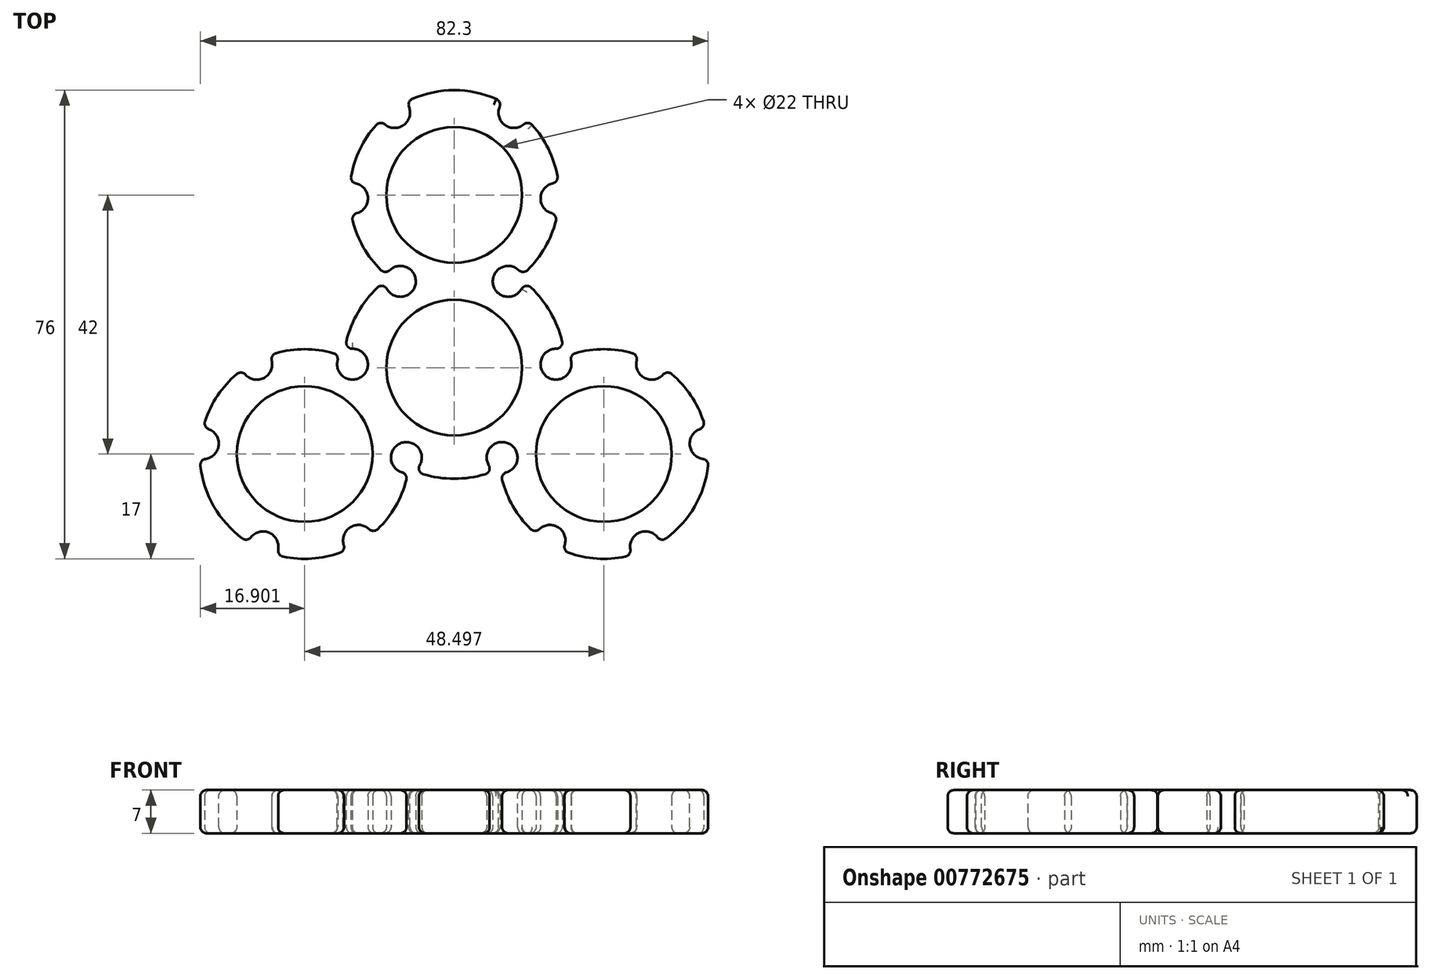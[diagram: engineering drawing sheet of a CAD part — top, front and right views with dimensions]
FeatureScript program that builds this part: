
annotation { "Feature Type Name" : "Feature", "Feature Type Description" : "" }
export const myFeature = defineFeature(function(context is Context, id is Id, definition is map)
    precondition{}
    {
        {
            var Q0;
            Q0=qCreatedBy(makeId("Top.planeOp"),FACE);
            var sketch = newSketch(context, id + "F0", { "sketchPlane" : qUnion([Q0])});
            skCircle(sketch, "E0", {"center": v(0, 0) * mm, "radius": 11 * mm});
            skCircle(sketch, "E1", {"center": v(0, 28) * mm, "radius": 11 * mm});
            skCircle(sketch, "E2", {"center": v(24.25, -14) * mm, "radius": 11 * mm});
            skCircle(sketch, "E3", {"center": v(-24.25, -14) * mm, "radius": 11 * mm});
            skLineSegment(sketch, "E4", {"start": v(0, 0) * mm, "end": v(0, 77.87) * mm, "construction": true});
            skLineSegment(sketch, "E5", {"start": v(0, 0) * mm, "end": v(69.01, -39.84) * mm, "construction": true});
            skLineSegment(sketch, "E6", {"start": v(0, 0) * mm, "end": v(-61.15, -35.3) * mm, "construction": true});
            skCircle(sketch, "E7", {"center": v(0, 0) * mm, "radius": 14 * mm});
            skCircle(sketch, "E8", {"center": v(0, 28) * mm, "radius": 14 * mm});
            skCircle(sketch, "E9", {"center": v(24.25, -14) * mm, "radius": 14 * mm});
            skCircle(sketch, "E10", {"center": v(-24.25, -14) * mm, "radius": 14 * mm});
            skArc(sketch, "E11", {"start": v(7.4, 16.12) * mm, "mid": v(6.23, 14) * mm, "end": v(7.4, 11.88) * mm});
            skArc(sketch, "E12", {"start": v(-7.4, 11.88) * mm, "mid": v(-6.23, 14) * mm, "end": v(-7.4, 16.12) * mm});
            skArc(sketch, "E13.1.0", {"start": v(-6.58, -12.36) * mm, "mid": v(-9, -12.4) * mm, "end": v(-10.26, -14.48) * mm});
            skArc(sketch, "E13.1.1", {"start": v(-17.67, -1.64) * mm, "mid": v(-15.24, -1.6) * mm, "end": v(-14, 0.48) * mm});
            skArc(sketch, "E13.2.0", {"start": v(14, 0.48) * mm, "mid": v(15.24, -1.6) * mm, "end": v(17.67, -1.64) * mm});
            skArc(sketch, "E13.2.1", {"start": v(10.26, -14.48) * mm, "mid": v(9, -12.4) * mm, "end": v(6.58, -12.36) * mm});
            skSolve(sketch);
        }
        {
            var Q0;
            Q0 = qSketchRegion(id + "F0", true);
            extrude(context, id + "F1", {"entities" : qUnion([Q0]), "depth" : 7 * mm, "offsetDistance" : 25 * mm});
        }
        {
            var Q0;
            Q0=makeQuery(id+"F1.opExtrude","CAP_FACE",FACE,{"disambiguationData":[OSD([sQuery(id+"F0.wireOp",EDGE,"E0"),sQuery(id+"F0.wireOp",EDGE,"E1"),sQuery(id+"F0.wireOp",EDGE,"E2"),sQuery(id+"F0.wireOp",EDGE,"E3"),sQuery(id+"F0.wireOp",EDGE,"E7"),sQuery(id+"F0.wireOp",EDGE,"E8"),sQuery(id+"F0.wireOp",EDGE,"E9"),sQuery(id+"F0.wireOp",EDGE,"E10"),sQuery(id+"F0.wireOp",EDGE,"E11"),sQuery(id+"F0.wireOp",EDGE,"E12"),sQuery(id+"F0.wireOp",EDGE,"E13.1.0"),sQuery(id+"F0.wireOp",EDGE,"E13.1.1"),sQuery(id+"F0.wireOp",EDGE,"E13.2.0"),sQuery(id+"F0.wireOp",EDGE,"E13.2.1")])],"isStart":false});
            var sketch = newSketch(context, id + "F2", { "sketchPlane" : qUnion([Q0])});
            skArc(sketch, "E14", {"start": v(7.4, 11.88) * mm, "mid": v(9.97, 11.83) * mm, "end": v(11.23, 14.07) * mm});
            skArc(sketch, "E15", {"start": v(17.8, 2.7) * mm, "mid": v(15.23, 2.72) * mm, "end": v(14, 0.48) * mm});
            skArc(sketch, "E16", {"start": v(17.8, 2.7) * mm, "mid": v(15.59, 9) * mm, "end": v(11.23, 14.07) * mm});
            skArc(sketch, "E17.1.0", {"start": v(-14, 0.48) * mm, "mid": v(-15.23, 2.72) * mm, "end": v(-17.8, 2.7) * mm});
            skArc(sketch, "E17.1.1", {"start": v(-11.23, 14.07) * mm, "mid": v(-15.59, 9) * mm, "end": v(-17.8, 2.7) * mm});
            skArc(sketch, "E17.1.2", {"start": v(-11.23, 14.07) * mm, "mid": v(-9.97, 11.83) * mm, "end": v(-7.4, 11.88) * mm});
            skArc(sketch, "E17.2.0", {"start": v(6.58, -12.36) * mm, "mid": v(5.26, -14.55) * mm, "end": v(6.57, -16.76) * mm});
            skArc(sketch, "E17.2.1", {"start": v(-6.57, -16.76) * mm, "mid": v(0, -18) * mm, "end": v(6.57, -16.76) * mm});
            skArc(sketch, "E17.2.2", {"start": v(-6.57, -16.76) * mm, "mid": v(-5.26, -14.55) * mm, "end": v(-6.58, -12.36) * mm});
            skCircle(sketch, "E18", {"center": v(0, 0) * mm, "radius": 14 * mm});
            skCircle(sketch, "E19", {"center": v(0, 0) * mm, "radius": 11.43 * mm});
            skSolve(sketch);
        }
        {
            var Q0;
            Q0 = qSketchRegion(id + "F2", true);
            extrude(context, id + "F3", {"entities" : qUnion([Q0]), "operationType" : NewBodyOperationType.ADD, "oppositeDirection" : true, "depth" : 7 * mm, "offsetDistance" : 25 * mm});
        }
        {
            var Q0;
            Q0=makeQuery(id+"F3.opExtrude","SWEPT_EDGE",EDGE,{"disambiguationData":[OSD([sQuery(id+"F2.wireOp",EDGE,"E17.1.1"),sQuery(id+"F2.wireOp",EDGE,"E17.1.2")])]});
            var Q1;
            Q1=makeQuery(id+"F3.opExtrude","SWEPT_EDGE",EDGE,{"disambiguationData":[OSD([sQuery(id+"F2.wireOp",EDGE,"E17.1.0"),sQuery(id+"F2.wireOp",EDGE,"E17.1.1")])]});
            var Q2;
            Q2=makeQuery(id+"F3.opExtrude","SWEPT_EDGE",EDGE,{"disambiguationData":[OSD([sQuery(id+"F2.wireOp",EDGE,"E17.2.1"),sQuery(id+"F2.wireOp",EDGE,"E17.2.2")])]});
            var Q3;
            Q3=makeQuery(id+"F3.opExtrude","SWEPT_EDGE",EDGE,{"disambiguationData":[OSD([sQuery(id+"F2.wireOp",EDGE,"E17.2.0"),sQuery(id+"F2.wireOp",EDGE,"E17.2.1")])]});
            var Q4;
            Q4=makeQuery(id+"F3.opExtrude","SWEPT_EDGE",EDGE,{"disambiguationData":[OSD([sQuery(id+"F2.wireOp",EDGE,"E15"),sQuery(id+"F2.wireOp",EDGE,"E16")])]});
            var Q5;
            Q5=makeQuery(id+"F3.opExtrude","SWEPT_EDGE",EDGE,{"disambiguationData":[OSD([sQuery(id+"F2.wireOp",EDGE,"E14"),sQuery(id+"F2.wireOp",EDGE,"E16")])]});
            fillet(context, id + "F4", {"entities" : qUnion([Q0, Q1, Q2, Q3, Q4, Q5]), "radius" : 1 * mm, "tangentPropagation" : true, "allowEdgeOverflow" : false});
        }
        {
            var Q0;
            Q0=makeQuery(id+"F3.boolean.opBoolean","MERGE",FACE,{"derivedFrom":[makeQuery(id+"F1.opExtrude","CAP_FACE",FACE,{"disambiguationData":[OSD([sQuery(id+"F0.wireOp",EDGE,"E0"),sQuery(id+"F0.wireOp",EDGE,"E1"),sQuery(id+"F0.wireOp",EDGE,"E2"),sQuery(id+"F0.wireOp",EDGE,"E3"),sQuery(id+"F0.wireOp",EDGE,"E7"),sQuery(id+"F0.wireOp",EDGE,"E8"),sQuery(id+"F0.wireOp",EDGE,"E9"),sQuery(id+"F0.wireOp",EDGE,"E10"),sQuery(id+"F0.wireOp",EDGE,"E11"),sQuery(id+"F0.wireOp",EDGE,"E12"),sQuery(id+"F0.wireOp",EDGE,"E13.1.0"),sQuery(id+"F0.wireOp",EDGE,"E13.1.1"),sQuery(id+"F0.wireOp",EDGE,"E13.2.0"),sQuery(id+"F0.wireOp",EDGE,"E13.2.1")])],"isStart":false}),makeQuery(id+"F3.opExtrude","CAP_FACE",FACE,{"disambiguationData":[OSD([sQuery(id+"F2.wireOp",EDGE,"E14"),sQuery(id+"F2.wireOp",EDGE,"E15"),sQuery(id+"F2.wireOp",EDGE,"E16"),sQuery(id+"F2.wireOp",EDGE,"E17.1.0"),sQuery(id+"F2.wireOp",EDGE,"E17.1.1"),sQuery(id+"F2.wireOp",EDGE,"E17.1.2"),sQuery(id+"F2.wireOp",EDGE,"E17.2.0"),sQuery(id+"F2.wireOp",EDGE,"E17.2.1"),sQuery(id+"F2.wireOp",EDGE,"E17.2.2"),sQuery(id+"F2.wireOp",EDGE,"E18"),sQuery(id+"F2.wireOp",EDGE,"E19")])],"isStart":true})]});
            var sketch = newSketch(context, id + "F5", { "sketchPlane" : qUnion([Q0])});
            skArc(sketch, "E20", {"start": v(-7.4, 16.12) * mm, "mid": v(-9.45, 16.4) * mm, "end": v(-11, 15.04) * mm});
            skArc(sketch, "E21", {"start": v(-16.72, 24.95) * mm, "mid": v(-14.78, 25.62) * mm, "end": v(-14, 27.52) * mm});
            skArc(sketch, "E22", {"start": v(-16.72, 24.95) * mm, "mid": v(-14.72, 19.5) * mm, "end": v(-11, 15.04) * mm});
            skArc(sketch, "E23.2.0", {"start": v(14, 27.52) * mm, "mid": v(14.78, 25.62) * mm, "end": v(16.72, 24.95) * mm});
            skArc(sketch, "E23.2.1", {"start": v(11, 15.04) * mm, "mid": v(14.72, 19.5) * mm, "end": v(16.72, 24.95) * mm});
            skArc(sketch, "E23.2.2", {"start": v(11, 15.04) * mm, "mid": v(9.45, 16.4) * mm, "end": v(7.4, 16.12) * mm});
            skArc(sketch, "E24", {"start": v(-7.4, 16.12) * mm, "mid": v(0, 14) * mm, "end": v(7.4, 16.12) * mm});
            skCircle(sketch, "E25", {"center": v(0, 28) * mm, "radius": 11.73 * mm});
            skArc(sketch, "E26", {"start": v(-14, 27.52) * mm, "mid": v(-14.9, 29.37) * mm, "end": v(-16.9, 29.9) * mm});
            skArc(sketch, "E27", {"start": v(16.9, 29.9) * mm, "mid": v(14.9, 29.37) * mm, "end": v(14, 27.52) * mm});
            skArc(sketch, "E28", {"start": v(-11.86, 40.18) * mm, "mid": v(-10.22, 38.94) * mm, "end": v(-8.2, 39.35) * mm});
            skArc(sketch, "E29", {"start": v(8.2, 39.35) * mm, "mid": v(10.22, 38.94) * mm, "end": v(11.86, 40.18) * mm});
            skArc(sketch, "E30", {"start": v(-11.86, 40.18) * mm, "mid": v(-15.27, 35.48) * mm, "end": v(-16.9, 29.9) * mm});
            skArc(sketch, "E31", {"start": v(16.9, 29.9) * mm, "mid": v(15.27, 35.48) * mm, "end": v(11.86, 40.18) * mm});
            skArc(sketch, "E32", {"start": v(7.84, 43.08) * mm, "mid": v(7.18, 41.13) * mm, "end": v(8.2, 39.35) * mm});
            skArc(sketch, "E33", {"start": v(-8.2, 39.35) * mm, "mid": v(-7.18, 41.13) * mm, "end": v(-7.84, 43.08) * mm});
            skArc(sketch, "E34", {"start": v(7.84, 43.08) * mm, "mid": v(0, 45) * mm, "end": v(-7.84, 43.08) * mm});
            skArc(sketch, "E35.1.0", {"start": v(-28.87, -30.36) * mm, "mid": v(-23.1, -30.96) * mm, "end": v(-17.45, -29.58) * mm});
            skCircle(sketch, "E35.1.1", {"center": v(-24.25, -14) * mm, "radius": 11.73 * mm});
            skArc(sketch, "E35.1.2", {"start": v(-28.87, -30.36) * mm, "mid": v(-28.6, -28.32) * mm, "end": v(-29.98, -26.78) * mm});
            skArc(sketch, "E35.1.3", {"start": v(-29.98, -26.78) * mm, "mid": v(-32.04, -26.78) * mm, "end": v(-33.4, -28.33) * mm});
            skArc(sketch, "E35.1.4", {"start": v(-41.23, -14.75) * mm, "mid": v(-38.97, -22.5) * mm, "end": v(-33.4, -28.33) * mm});
            skArc(sketch, "E35.1.5", {"start": v(-41.23, -14.75) * mm, "mid": v(-39.21, -14.35) * mm, "end": v(-38.18, -12.57) * mm});
            skArc(sketch, "E35.1.6", {"start": v(-38.18, -12.57) * mm, "mid": v(-38.83, -10.62) * mm, "end": v(-40.73, -9.82) * mm});
            skArc(sketch, "E35.1.7", {"start": v(-34.35, -0.32) * mm, "mid": v(-38.36, -4.52) * mm, "end": v(-40.73, -9.82) * mm});
            skArc(sketch, "E35.1.8", {"start": v(-34.35, -0.32) * mm, "mid": v(-32.89, -1.78) * mm, "end": v(-30.83, -1.64) * mm});
            skArc(sketch, "E35.1.9", {"start": v(-30.83, -1.64) * mm, "mid": v(-29.57, -0.01) * mm, "end": v(-29.97, 2) * mm});
            skArc(sketch, "E35.1.10", {"start": v(-18.53, 2) * mm, "mid": v(-24.25, 3) * mm, "end": v(-29.97, 2) * mm});
            skArc(sketch, "E35.1.11", {"start": v(-18.53, 2) * mm, "mid": v(-18.92, -0.01) * mm, "end": v(-17.67, -1.64) * mm});
            skArc(sketch, "E35.1.12", {"start": v(-10.26, -14.48) * mm, "mid": v(-12.12, -7) * mm, "end": v(-17.67, -1.64) * mm});
            skArc(sketch, "E35.1.13", {"start": v(-10.26, -14.48) * mm, "mid": v(-9.47, -16.38) * mm, "end": v(-7.52, -17.05) * mm});
            skArc(sketch, "E35.1.14", {"start": v(-13.24, -26.96) * mm, "mid": v(-9.53, -22.5) * mm, "end": v(-7.52, -17.05) * mm});
            skArc(sketch, "E35.1.15", {"start": v(-13.24, -26.96) * mm, "mid": v(-14.8, -25.6) * mm, "end": v(-16.84, -25.88) * mm});
            skArc(sketch, "E35.1.16", {"start": v(-16.84, -25.88) * mm, "mid": v(-17.98, -27.6) * mm, "end": v(-17.45, -29.58) * mm});
            skArc(sketch, "E35.2.0", {"start": v(40.73, -9.82) * mm, "mid": v(38.36, -4.52) * mm, "end": v(34.35, -0.32) * mm});
            skCircle(sketch, "E35.2.1", {"center": v(24.25, -14) * mm, "radius": 11.73 * mm});
            skArc(sketch, "E35.2.2", {"start": v(40.73, -9.82) * mm, "mid": v(38.83, -10.62) * mm, "end": v(38.18, -12.57) * mm});
            skArc(sketch, "E35.2.3", {"start": v(38.18, -12.57) * mm, "mid": v(39.21, -14.35) * mm, "end": v(41.23, -14.75) * mm});
            skArc(sketch, "E35.2.4", {"start": v(33.4, -28.33) * mm, "mid": v(38.97, -22.5) * mm, "end": v(41.23, -14.75) * mm});
            skArc(sketch, "E35.2.5", {"start": v(33.4, -28.33) * mm, "mid": v(32.03, -26.78) * mm, "end": v(29.98, -26.78) * mm});
            skArc(sketch, "E35.2.6", {"start": v(29.98, -26.78) * mm, "mid": v(28.6, -28.32) * mm, "end": v(28.86, -30.36) * mm});
            skArc(sketch, "E35.2.7", {"start": v(17.45, -29.58) * mm, "mid": v(23.1, -30.96) * mm, "end": v(28.86, -30.36) * mm});
            skArc(sketch, "E35.2.8", {"start": v(17.45, -29.58) * mm, "mid": v(17.98, -27.6) * mm, "end": v(16.84, -25.88) * mm});
            skArc(sketch, "E35.2.9", {"start": v(16.84, -25.88) * mm, "mid": v(14.8, -25.6) * mm, "end": v(13.24, -26.96) * mm});
            skArc(sketch, "E35.2.10", {"start": v(7.52, -17.05) * mm, "mid": v(9.53, -22.5) * mm, "end": v(13.24, -26.96) * mm});
            skArc(sketch, "E35.2.11", {"start": v(7.52, -17.05) * mm, "mid": v(9.47, -16.38) * mm, "end": v(10.26, -14.48) * mm});
            skArc(sketch, "E35.2.12", {"start": v(17.67, -1.64) * mm, "mid": v(12.12, -7) * mm, "end": v(10.26, -14.48) * mm});
            skArc(sketch, "E35.2.13", {"start": v(17.67, -1.64) * mm, "mid": v(18.92, -0.01) * mm, "end": v(18.53, 2) * mm});
            skArc(sketch, "E35.2.14", {"start": v(29.97, 2) * mm, "mid": v(24.25, 3) * mm, "end": v(18.53, 2) * mm});
            skArc(sketch, "E35.2.15", {"start": v(29.97, 2) * mm, "mid": v(29.57, -0.01) * mm, "end": v(30.83, -1.64) * mm});
            skArc(sketch, "E35.2.16", {"start": v(30.83, -1.64) * mm, "mid": v(32.89, -1.78) * mm, "end": v(34.35, -0.32) * mm});
            skPoint(sketch, "E35.center", {"position": v(0, 0) * mm});
            skSolve(sketch);
        }
        {
            var Q0;
            Q0 = qSketchRegion(id + "F5", true);
            extrude(context, id + "F6", {"entities" : qUnion([Q0]), "operationType" : NewBodyOperationType.ADD, "oppositeDirection" : true, "depth" : 7 * mm, "offsetDistance" : 25 * mm});
        }
        {
            var Q0;
            Q0=makeQuery(id+"F6.opExtrude","SWEPT_EDGE",EDGE,{"disambiguationData":[OSD([sQuery(id+"F5.wireOp",EDGE,"E20"),sQuery(id+"F5.wireOp",EDGE,"E22")])]});
            var Q1;
            Q1=makeQuery(id+"F6.opExtrude","SWEPT_EDGE",EDGE,{"disambiguationData":[OSD([sQuery(id+"F5.wireOp",EDGE,"E26"),sQuery(id+"F5.wireOp",EDGE,"E30")])]});
            var Q2;
            Q2=makeQuery(id+"F6.opExtrude","SWEPT_EDGE",EDGE,{"disambiguationData":[OSD([sQuery(id+"F5.wireOp",EDGE,"E23.2.1"),sQuery(id+"F5.wireOp",EDGE,"E23.2.2")])]});
            var Q3;
            Q3=makeQuery(id+"F6.opExtrude","SWEPT_EDGE",EDGE,{"disambiguationData":[OSD([sQuery(id+"F5.wireOp",EDGE,"E27"),sQuery(id+"F5.wireOp",EDGE,"E31")])]});
            var Q4;
            Q4=makeQuery(id+"F6.opExtrude","SWEPT_EDGE",EDGE,{"disambiguationData":[OSD([sQuery(id+"F5.wireOp",EDGE,"E21"),sQuery(id+"F5.wireOp",EDGE,"E22")])]});
            var Q5;
            Q5=makeQuery(id+"F6.opExtrude","SWEPT_EDGE",EDGE,{"disambiguationData":[OSD([sQuery(id+"F5.wireOp",EDGE,"E23.2.0"),sQuery(id+"F5.wireOp",EDGE,"E23.2.1")])]});
            var Q6;
            Q6=makeQuery(id+"F6.opExtrude","SWEPT_EDGE",EDGE,{"disambiguationData":[OSD([sQuery(id+"F5.wireOp",EDGE,"E33"),sQuery(id+"F5.wireOp",EDGE,"E34")])]});
            var Q7;
            Q7=makeQuery(id+"F6.opExtrude","SWEPT_EDGE",EDGE,{"disambiguationData":[OSD([sQuery(id+"F5.wireOp",EDGE,"E32"),sQuery(id+"F5.wireOp",EDGE,"E34")])]});
            var Q8;
            Q8=makeQuery(id+"F6.opExtrude","SWEPT_EDGE",EDGE,{"disambiguationData":[OSD([sQuery(id+"F5.wireOp",EDGE,"E29"),sQuery(id+"F5.wireOp",EDGE,"E31")])]});
            var Q9;
            Q9=makeQuery(id+"F6.opExtrude","SWEPT_EDGE",EDGE,{"disambiguationData":[OSD([sQuery(id+"F5.wireOp",EDGE,"E28"),sQuery(id+"F5.wireOp",EDGE,"E30")])]});
            var Q10;
            Q10=makeQuery(id+"F6.opExtrude","SWEPT_EDGE",EDGE,{"disambiguationData":[OSD([sQuery(id+"F5.wireOp",EDGE,"E35.2.13"),sQuery(id+"F5.wireOp",EDGE,"E35.2.14")])]});
            var Q11;
            Q11=makeQuery(id+"F6.opExtrude","SWEPT_EDGE",EDGE,{"disambiguationData":[OSD([sQuery(id+"F5.wireOp",EDGE,"E35.2.14"),sQuery(id+"F5.wireOp",EDGE,"E35.2.15")])]});
            var Q12;
            Q12=makeQuery(id+"F6.opExtrude","SWEPT_EDGE",EDGE,{"disambiguationData":[OSD([sQuery(id+"F5.wireOp",EDGE,"E35.2.0"),sQuery(id+"F5.wireOp",EDGE,"E35.2.16")])]});
            var Q13;
            Q13=makeQuery(id+"F6.opExtrude","SWEPT_EDGE",EDGE,{"disambiguationData":[OSD([sQuery(id+"F5.wireOp",EDGE,"E35.2.0"),sQuery(id+"F5.wireOp",EDGE,"E35.2.2")])]});
            var Q14;
            Q14=makeQuery(id+"F6.opExtrude","SWEPT_EDGE",EDGE,{"disambiguationData":[OSD([sQuery(id+"F5.wireOp",EDGE,"E35.2.3"),sQuery(id+"F5.wireOp",EDGE,"E35.2.4")])]});
            var Q15;
            Q15=makeQuery(id+"F6.opExtrude","SWEPT_EDGE",EDGE,{"disambiguationData":[OSD([sQuery(id+"F5.wireOp",EDGE,"E35.2.4"),sQuery(id+"F5.wireOp",EDGE,"E35.2.5")])]});
            var Q16;
            Q16=makeQuery(id+"F6.opExtrude","SWEPT_EDGE",EDGE,{"disambiguationData":[OSD([sQuery(id+"F5.wireOp",EDGE,"E35.2.6"),sQuery(id+"F5.wireOp",EDGE,"E35.2.7")])]});
            var Q17;
            Q17=makeQuery(id+"F6.opExtrude","SWEPT_EDGE",EDGE,{"disambiguationData":[OSD([sQuery(id+"F5.wireOp",EDGE,"E35.2.7"),sQuery(id+"F5.wireOp",EDGE,"E35.2.8")])]});
            var Q18;
            Q18=makeQuery(id+"F6.opExtrude","SWEPT_EDGE",EDGE,{"disambiguationData":[OSD([sQuery(id+"F5.wireOp",EDGE,"E35.2.9"),sQuery(id+"F5.wireOp",EDGE,"E35.2.10")])]});
            var Q19;
            Q19=makeQuery(id+"F6.opExtrude","SWEPT_EDGE",EDGE,{"disambiguationData":[OSD([sQuery(id+"F5.wireOp",EDGE,"E35.2.10"),sQuery(id+"F5.wireOp",EDGE,"E35.2.11")])]});
            var Q20;
            Q20=makeQuery(id+"F6.opExtrude","SWEPT_EDGE",EDGE,{"disambiguationData":[OSD([sQuery(id+"F5.wireOp",EDGE,"E35.1.13"),sQuery(id+"F5.wireOp",EDGE,"E35.1.14")])]});
            var Q21;
            Q21=makeQuery(id+"F6.opExtrude","SWEPT_EDGE",EDGE,{"disambiguationData":[OSD([sQuery(id+"F5.wireOp",EDGE,"E35.1.14"),sQuery(id+"F5.wireOp",EDGE,"E35.1.15")])]});
            var Q22;
            Q22=makeQuery(id+"F6.opExtrude","SWEPT_EDGE",EDGE,{"disambiguationData":[OSD([sQuery(id+"F5.wireOp",EDGE,"E35.1.0"),sQuery(id+"F5.wireOp",EDGE,"E35.1.16")])]});
            var Q23;
            Q23=makeQuery(id+"F6.opExtrude","SWEPT_EDGE",EDGE,{"disambiguationData":[OSD([sQuery(id+"F5.wireOp",EDGE,"E35.1.0"),sQuery(id+"F5.wireOp",EDGE,"E35.1.2")])]});
            var Q24;
            Q24=makeQuery(id+"F6.opExtrude","SWEPT_EDGE",EDGE,{"disambiguationData":[OSD([sQuery(id+"F5.wireOp",EDGE,"E35.1.3"),sQuery(id+"F5.wireOp",EDGE,"E35.1.4")])]});
            var Q25;
            Q25=makeQuery(id+"F6.opExtrude","SWEPT_EDGE",EDGE,{"disambiguationData":[OSD([sQuery(id+"F5.wireOp",EDGE,"E35.1.4"),sQuery(id+"F5.wireOp",EDGE,"E35.1.5")])]});
            var Q26;
            Q26=makeQuery(id+"F6.opExtrude","SWEPT_EDGE",EDGE,{"disambiguationData":[OSD([sQuery(id+"F5.wireOp",EDGE,"E35.1.6"),sQuery(id+"F5.wireOp",EDGE,"E35.1.7")])]});
            var Q27;
            Q27=makeQuery(id+"F6.opExtrude","SWEPT_EDGE",EDGE,{"disambiguationData":[OSD([sQuery(id+"F5.wireOp",EDGE,"E35.1.7"),sQuery(id+"F5.wireOp",EDGE,"E35.1.8")])]});
            var Q28;
            Q28=makeQuery(id+"F6.opExtrude","SWEPT_EDGE",EDGE,{"disambiguationData":[OSD([sQuery(id+"F5.wireOp",EDGE,"E35.1.9"),sQuery(id+"F5.wireOp",EDGE,"E35.1.10")])]});
            var Q29;
            Q29=makeQuery(id+"F6.opExtrude","SWEPT_EDGE",EDGE,{"disambiguationData":[OSD([sQuery(id+"F5.wireOp",EDGE,"E35.1.10"),sQuery(id+"F5.wireOp",EDGE,"E35.1.11")])]});
            fillet(context, id + "F7", {"entities" : qUnion([Q0, Q1, Q2, Q3, Q4, Q5, Q6, Q7, Q8, Q9, Q10, Q11, Q12, Q13, Q14, Q15, Q16, Q17, Q18, Q19, Q20, Q21, Q22, Q23, Q24, Q25, Q26, Q27, Q28, Q29]), "radius" : 1 * mm, "tangentPropagation" : true, "allowEdgeOverflow" : false});
        }
        {
            var Q0;
            Q0=makeQuery(id+"F6.boolean.opBoolean","MERGE",FACE,{"derivedFrom":[makeQuery(id+"F3.boolean.opBoolean","MERGE",FACE,{"derivedFrom":[makeQuery(id+"F1.opExtrude","CAP_FACE",FACE,{"disambiguationData":[OSD([sQuery(id+"F0.wireOp",EDGE,"E0"),sQuery(id+"F0.wireOp",EDGE,"E1"),sQuery(id+"F0.wireOp",EDGE,"E2"),sQuery(id+"F0.wireOp",EDGE,"E3"),sQuery(id+"F0.wireOp",EDGE,"E7"),sQuery(id+"F0.wireOp",EDGE,"E8"),sQuery(id+"F0.wireOp",EDGE,"E9"),sQuery(id+"F0.wireOp",EDGE,"E10"),sQuery(id+"F0.wireOp",EDGE,"E11"),sQuery(id+"F0.wireOp",EDGE,"E12"),sQuery(id+"F0.wireOp",EDGE,"E13.1.0"),sQuery(id+"F0.wireOp",EDGE,"E13.1.1"),sQuery(id+"F0.wireOp",EDGE,"E13.2.0"),sQuery(id+"F0.wireOp",EDGE,"E13.2.1")])],"isStart":false}),makeQuery(id+"F3.opExtrude","CAP_FACE",FACE,{"disambiguationData":[OSD([sQuery(id+"F2.wireOp",EDGE,"E14"),sQuery(id+"F2.wireOp",EDGE,"E15"),sQuery(id+"F2.wireOp",EDGE,"E16"),sQuery(id+"F2.wireOp",EDGE,"E17.1.0"),sQuery(id+"F2.wireOp",EDGE,"E17.1.1"),sQuery(id+"F2.wireOp",EDGE,"E17.1.2"),sQuery(id+"F2.wireOp",EDGE,"E17.2.0"),sQuery(id+"F2.wireOp",EDGE,"E17.2.1"),sQuery(id+"F2.wireOp",EDGE,"E17.2.2"),sQuery(id+"F2.wireOp",EDGE,"E18"),sQuery(id+"F2.wireOp",EDGE,"E19")])],"isStart":true})]}),makeQuery(id+"F6.opExtrude","CAP_FACE",FACE,{"disambiguationData":[OSD([sQuery(id+"F5.wireOp",EDGE,"E20"),sQuery(id+"F5.wireOp",EDGE,"E21"),sQuery(id+"F5.wireOp",EDGE,"E22"),sQuery(id+"F5.wireOp",EDGE,"E23.2.0"),sQuery(id+"F5.wireOp",EDGE,"E23.2.1"),sQuery(id+"F5.wireOp",EDGE,"E23.2.2"),sQuery(id+"F5.wireOp",EDGE,"E24"),sQuery(id+"F5.wireOp",EDGE,"E25"),sQuery(id+"F5.wireOp",EDGE,"E26"),sQuery(id+"F5.wireOp",EDGE,"E27"),sQuery(id+"F5.wireOp",EDGE,"E28"),sQuery(id+"F5.wireOp",EDGE,"E29"),sQuery(id+"F5.wireOp",EDGE,"E30"),sQuery(id+"F5.wireOp",EDGE,"E31"),sQuery(id+"F5.wireOp",EDGE,"E32"),sQuery(id+"F5.wireOp",EDGE,"E33"),sQuery(id+"F5.wireOp",EDGE,"E34")])],"isStart":true}),makeQuery(id+"F6.opExtrude","CAP_FACE",FACE,{"disambiguationData":[OSD([sQuery(id+"F5.wireOp",EDGE,"E35.1.0"),sQuery(id+"F5.wireOp",EDGE,"E35.1.1"),sQuery(id+"F5.wireOp",EDGE,"E35.1.2"),sQuery(id+"F5.wireOp",EDGE,"E35.1.3"),sQuery(id+"F5.wireOp",EDGE,"E35.1.4"),sQuery(id+"F5.wireOp",EDGE,"E35.1.5"),sQuery(id+"F5.wireOp",EDGE,"E35.1.6"),sQuery(id+"F5.wireOp",EDGE,"E35.1.7"),sQuery(id+"F5.wireOp",EDGE,"E35.1.8"),sQuery(id+"F5.wireOp",EDGE,"E35.1.9"),sQuery(id+"F5.wireOp",EDGE,"E35.1.10"),sQuery(id+"F5.wireOp",EDGE,"E35.1.11"),sQuery(id+"F5.wireOp",EDGE,"E35.1.12"),sQuery(id+"F5.wireOp",EDGE,"E35.1.13"),sQuery(id+"F5.wireOp",EDGE,"E35.1.14"),sQuery(id+"F5.wireOp",EDGE,"E35.1.15"),sQuery(id+"F5.wireOp",EDGE,"E35.1.16")])],"isStart":true}),makeQuery(id+"F6.opExtrude","CAP_FACE",FACE,{"disambiguationData":[OSD([sQuery(id+"F5.wireOp",EDGE,"E35.2.0"),sQuery(id+"F5.wireOp",EDGE,"E35.2.1"),sQuery(id+"F5.wireOp",EDGE,"E35.2.2"),sQuery(id+"F5.wireOp",EDGE,"E35.2.3"),sQuery(id+"F5.wireOp",EDGE,"E35.2.4"),sQuery(id+"F5.wireOp",EDGE,"E35.2.5"),sQuery(id+"F5.wireOp",EDGE,"E35.2.6"),sQuery(id+"F5.wireOp",EDGE,"E35.2.7"),sQuery(id+"F5.wireOp",EDGE,"E35.2.8"),sQuery(id+"F5.wireOp",EDGE,"E35.2.9"),sQuery(id+"F5.wireOp",EDGE,"E35.2.10"),sQuery(id+"F5.wireOp",EDGE,"E35.2.11"),sQuery(id+"F5.wireOp",EDGE,"E35.2.12"),sQuery(id+"F5.wireOp",EDGE,"E35.2.13"),sQuery(id+"F5.wireOp",EDGE,"E35.2.14"),sQuery(id+"F5.wireOp",EDGE,"E35.2.15"),sQuery(id+"F5.wireOp",EDGE,"E35.2.16")])],"isStart":true})]});
            var Q1;
            Q1=makeQuery(id+"F6.boolean.opBoolean","MERGE",FACE,{"derivedFrom":[makeQuery(id+"F3.boolean.opBoolean","MERGE",FACE,{"derivedFrom":[makeQuery(id+"F1.opExtrude","CAP_FACE",FACE,{"disambiguationData":[OSD([sQuery(id+"F0.wireOp",EDGE,"E0"),sQuery(id+"F0.wireOp",EDGE,"E1"),sQuery(id+"F0.wireOp",EDGE,"E2"),sQuery(id+"F0.wireOp",EDGE,"E3"),sQuery(id+"F0.wireOp",EDGE,"E7"),sQuery(id+"F0.wireOp",EDGE,"E8"),sQuery(id+"F0.wireOp",EDGE,"E9"),sQuery(id+"F0.wireOp",EDGE,"E10"),sQuery(id+"F0.wireOp",EDGE,"E11"),sQuery(id+"F0.wireOp",EDGE,"E12"),sQuery(id+"F0.wireOp",EDGE,"E13.1.0"),sQuery(id+"F0.wireOp",EDGE,"E13.1.1"),sQuery(id+"F0.wireOp",EDGE,"E13.2.0"),sQuery(id+"F0.wireOp",EDGE,"E13.2.1")])],"isStart":true}),makeQuery(id+"F3.opExtrude","CAP_FACE",FACE,{"disambiguationData":[OSD([sQuery(id+"F2.wireOp",EDGE,"E14"),sQuery(id+"F2.wireOp",EDGE,"E15"),sQuery(id+"F2.wireOp",EDGE,"E16"),sQuery(id+"F2.wireOp",EDGE,"E17.1.0"),sQuery(id+"F2.wireOp",EDGE,"E17.1.1"),sQuery(id+"F2.wireOp",EDGE,"E17.1.2"),sQuery(id+"F2.wireOp",EDGE,"E17.2.0"),sQuery(id+"F2.wireOp",EDGE,"E17.2.1"),sQuery(id+"F2.wireOp",EDGE,"E17.2.2"),sQuery(id+"F2.wireOp",EDGE,"E18"),sQuery(id+"F2.wireOp",EDGE,"E19")])],"isStart":false})]}),makeQuery(id+"F6.opExtrude","CAP_FACE",FACE,{"disambiguationData":[OSD([sQuery(id+"F5.wireOp",EDGE,"E20"),sQuery(id+"F5.wireOp",EDGE,"E21"),sQuery(id+"F5.wireOp",EDGE,"E22"),sQuery(id+"F5.wireOp",EDGE,"E23.2.0"),sQuery(id+"F5.wireOp",EDGE,"E23.2.1"),sQuery(id+"F5.wireOp",EDGE,"E23.2.2"),sQuery(id+"F5.wireOp",EDGE,"E24"),sQuery(id+"F5.wireOp",EDGE,"E25"),sQuery(id+"F5.wireOp",EDGE,"E26"),sQuery(id+"F5.wireOp",EDGE,"E27"),sQuery(id+"F5.wireOp",EDGE,"E28"),sQuery(id+"F5.wireOp",EDGE,"E29"),sQuery(id+"F5.wireOp",EDGE,"E30"),sQuery(id+"F5.wireOp",EDGE,"E31"),sQuery(id+"F5.wireOp",EDGE,"E32"),sQuery(id+"F5.wireOp",EDGE,"E33"),sQuery(id+"F5.wireOp",EDGE,"E34")])],"isStart":false}),makeQuery(id+"F6.opExtrude","CAP_FACE",FACE,{"disambiguationData":[OSD([sQuery(id+"F5.wireOp",EDGE,"E35.1.0"),sQuery(id+"F5.wireOp",EDGE,"E35.1.1"),sQuery(id+"F5.wireOp",EDGE,"E35.1.2"),sQuery(id+"F5.wireOp",EDGE,"E35.1.3"),sQuery(id+"F5.wireOp",EDGE,"E35.1.4"),sQuery(id+"F5.wireOp",EDGE,"E35.1.5"),sQuery(id+"F5.wireOp",EDGE,"E35.1.6"),sQuery(id+"F5.wireOp",EDGE,"E35.1.7"),sQuery(id+"F5.wireOp",EDGE,"E35.1.8"),sQuery(id+"F5.wireOp",EDGE,"E35.1.9"),sQuery(id+"F5.wireOp",EDGE,"E35.1.10"),sQuery(id+"F5.wireOp",EDGE,"E35.1.11"),sQuery(id+"F5.wireOp",EDGE,"E35.1.12"),sQuery(id+"F5.wireOp",EDGE,"E35.1.13"),sQuery(id+"F5.wireOp",EDGE,"E35.1.14"),sQuery(id+"F5.wireOp",EDGE,"E35.1.15"),sQuery(id+"F5.wireOp",EDGE,"E35.1.16")])],"isStart":false}),makeQuery(id+"F6.opExtrude","CAP_FACE",FACE,{"disambiguationData":[OSD([sQuery(id+"F5.wireOp",EDGE,"E35.2.0"),sQuery(id+"F5.wireOp",EDGE,"E35.2.1"),sQuery(id+"F5.wireOp",EDGE,"E35.2.2"),sQuery(id+"F5.wireOp",EDGE,"E35.2.3"),sQuery(id+"F5.wireOp",EDGE,"E35.2.4"),sQuery(id+"F5.wireOp",EDGE,"E35.2.5"),sQuery(id+"F5.wireOp",EDGE,"E35.2.6"),sQuery(id+"F5.wireOp",EDGE,"E35.2.7"),sQuery(id+"F5.wireOp",EDGE,"E35.2.8"),sQuery(id+"F5.wireOp",EDGE,"E35.2.9"),sQuery(id+"F5.wireOp",EDGE,"E35.2.10"),sQuery(id+"F5.wireOp",EDGE,"E35.2.11"),sQuery(id+"F5.wireOp",EDGE,"E35.2.12"),sQuery(id+"F5.wireOp",EDGE,"E35.2.13"),sQuery(id+"F5.wireOp",EDGE,"E35.2.14"),sQuery(id+"F5.wireOp",EDGE,"E35.2.15"),sQuery(id+"F5.wireOp",EDGE,"E35.2.16")])],"isStart":false})]});
            fillet(context, id + "F8", {"entities" : qUnion([Q0, Q1]), "radius" : 1 * mm, "tangentPropagation" : true, "allowEdgeOverflow" : false});
        }
    });
